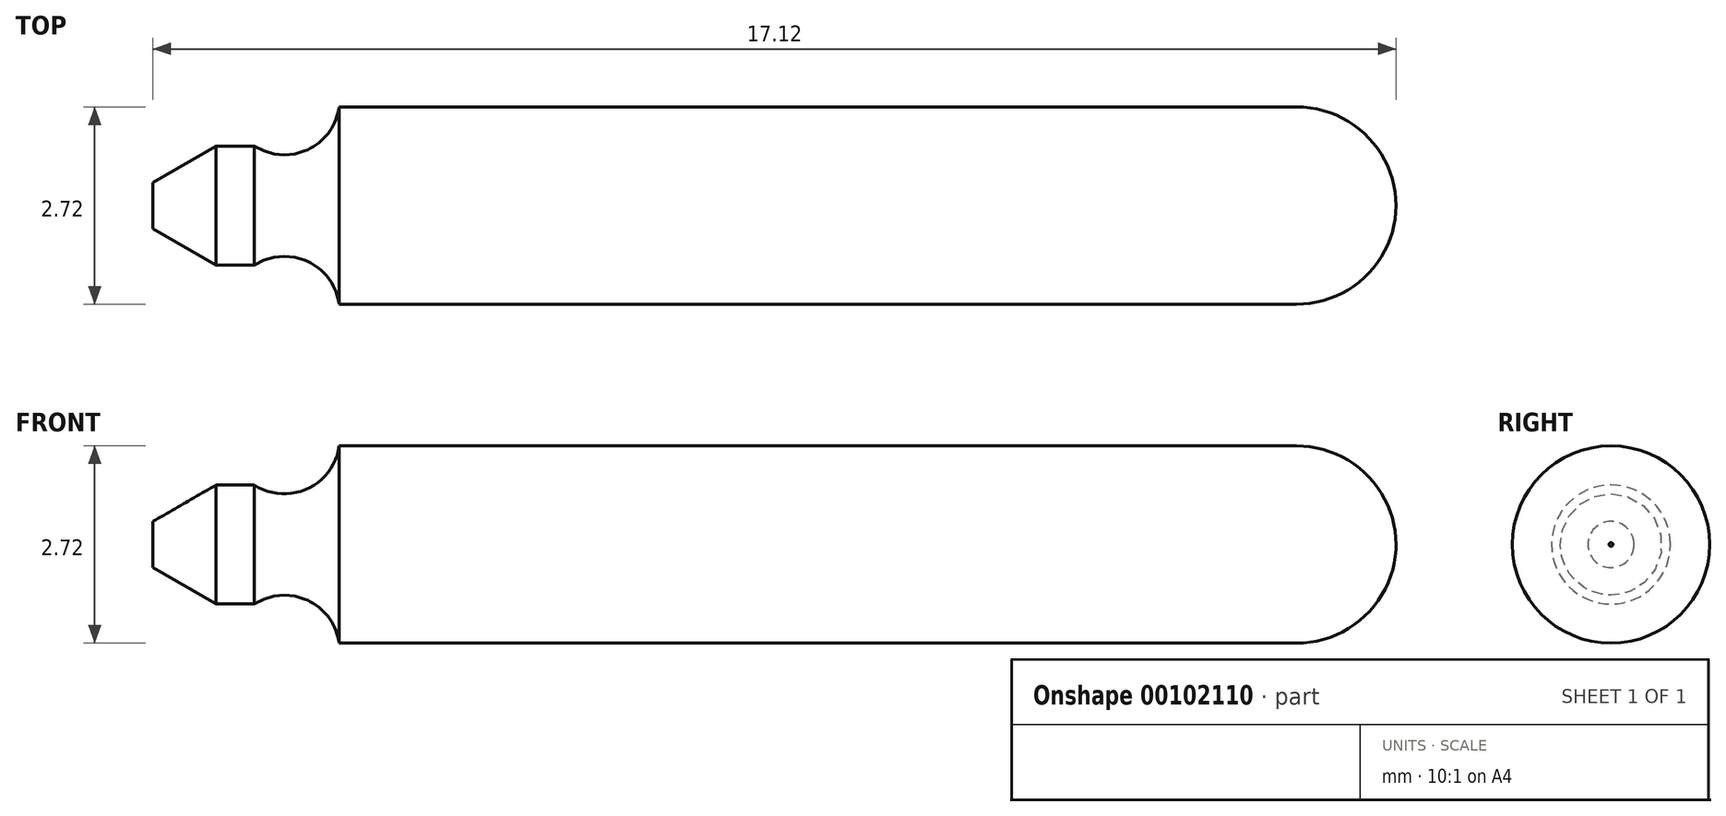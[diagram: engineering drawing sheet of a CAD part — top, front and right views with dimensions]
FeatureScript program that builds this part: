
annotation { "Feature Type Name" : "Feature", "Feature Type Description" : "" }
export const myFeature = defineFeature(function(context is Context, id is Id, definition is map)
    precondition{}
    {
        {
            var Q0;
            Q0=qCreatedBy(makeId("Front.planeOp"),FACE);
            var sketch = newSketch(context, id + "F0", { "sketchPlane" : qUnion([Q0])});
            skLineSegment(sketch, "E0", {"start": v(5.02, 0) * mm, "end": v(-10.73, 0) * mm});
            skLineSegment(sketch, "E1", {"start": v(5.02, 0) * mm, "end": v(5.02, 1.36) * mm});
            skLineSegment(sketch, "E2", {"start": v(5.02, 1.36) * mm, "end": v(-8.16, 1.36) * mm});
            skLineSegment(sketch, "E3", {"start": v(-10.73, 0) * mm, "end": v(-10.73, 0.32) * mm});
            skLineSegment(sketch, "E4", {"start": v(-10.73, 0.32) * mm, "end": v(-9.86, 0.82) * mm});
            skLineSegment(sketch, "E5", {"start": v(-9.86, 0.82) * mm, "end": v(-9.33, 0.82) * mm});
            skArc(sketch, "E6", {"start": v(-9.33, 0.82) * mm, "mid": v(-8.6, 0.77) * mm, "end": v(-8.16, 1.36) * mm});
            skLineSegment(sketch, "E7", {"start": v(5.02, 0) * mm, "end": v(6.4, 0) * mm});
            skArc(sketch, "E8", {"start": v(6.4, 0) * mm, "mid": v(5.99, 0.96) * mm, "end": v(5.02, 1.36) * mm});
            skSolve(sketch);
        }
        {
            var Q0;
            Q0=makeQuery(id+"F0.imprint","IMPRINT",FACE,{"disambiguationData":[TD([[makeQuery(id+"F0.imprint","IMPRINT",EDGE,{"derivedFrom":sQuery(id+"F0.wireOp",EDGE,"E0")}),-1.0]])]});
            var Q1;
            Q1=makeQuery(id+"F0.imprint","IMPRINT",FACE,{"disambiguationData":[TD([[makeQuery(id+"F0.imprint","IMPRINT",EDGE,{"derivedFrom":sQuery(id+"F0.wireOp",EDGE,"E1")}),-1.0]])]});
            var Q2;
            Q2=sQuery(id+"F0.wireOp",EDGE,"E7");
            revolve(context, id + "F1", {"entities" : qUnion([Q0, Q1]), "axis" : qUnion([Q2]), "revolveType" : RevolveType.FULL});
        }
    });
